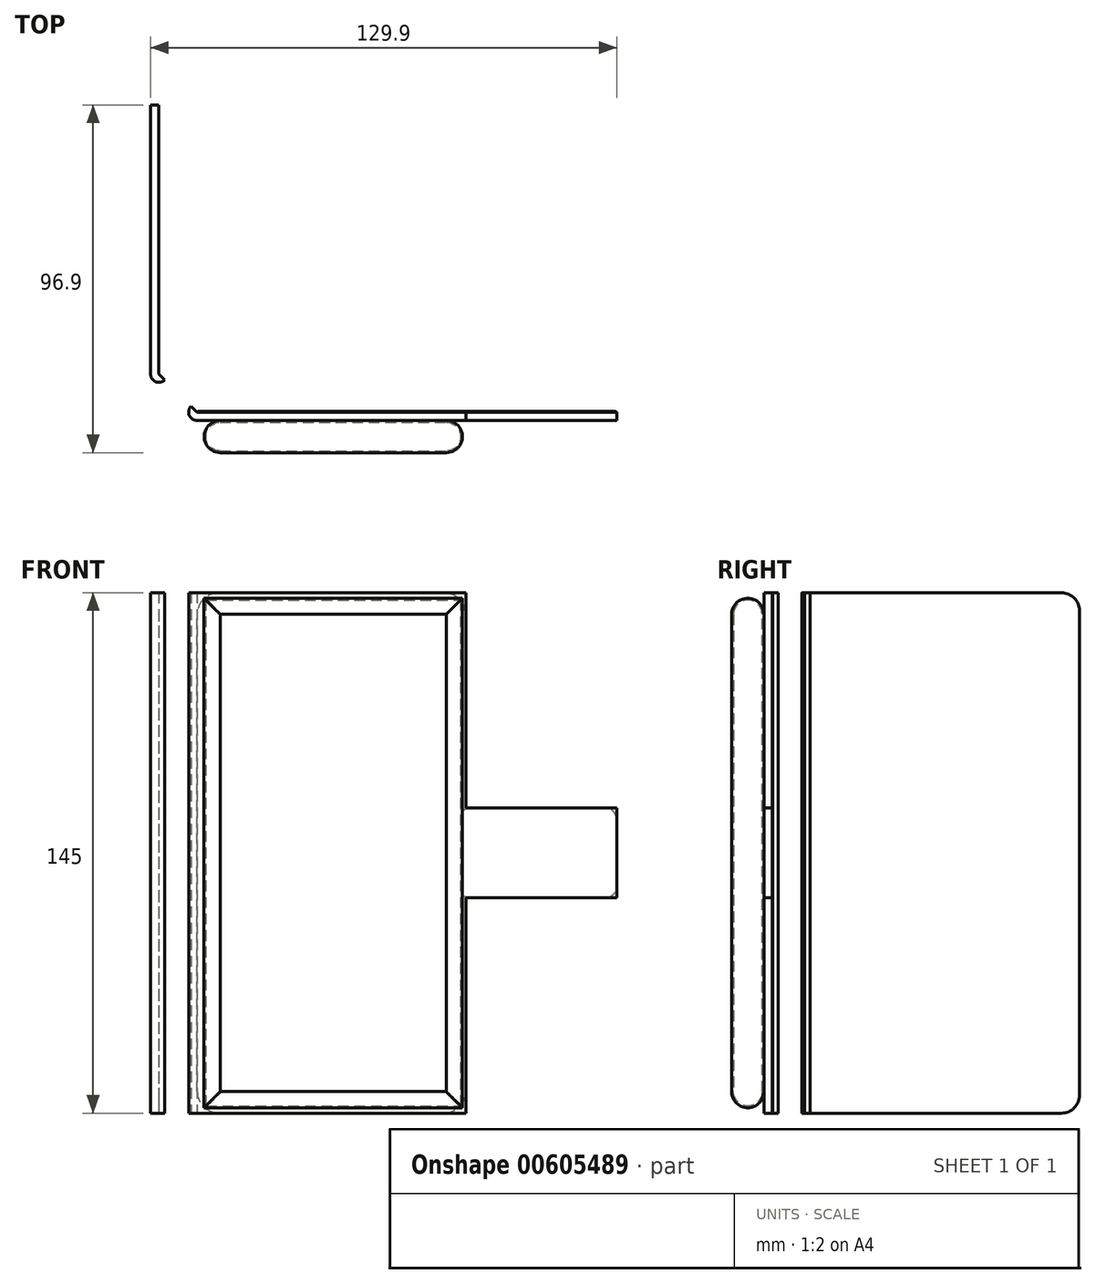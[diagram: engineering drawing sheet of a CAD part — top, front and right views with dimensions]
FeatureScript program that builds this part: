
annotation { "Feature Type Name" : "Feature", "Feature Type Description" : "" }
export const myFeature = defineFeature(function(context is Context, id is Id, definition is map)
    precondition{}
    {
        {
            var Q0;
            Q0=qCreatedBy(makeId("Front.planeOp"),FACE);
            var sketch = newSketch(context, id + "F0", { "sketchPlane" : qUnion([Q0])});
            skLineSegment(sketch, "E0.bottom", {"start": v(36, -71) * mm, "end": v(-36, -71) * mm});
            skLineSegment(sketch, "E0.top", {"start": v(36, 71) * mm, "end": v(-36, 71) * mm});
            skLineSegment(sketch, "E0.left", {"start": v(36, -71) * mm, "end": v(36, 71) * mm});
            skLineSegment(sketch, "E0.right", {"start": v(-36, -71) * mm, "end": v(-36, 71) * mm});
            skPoint(sketch, "E0.middle", {"position": v(0, 0) * mm});
            skSolve(sketch);
        }
        {
            var Q0;
            Q0=makeQuery(id+"F0.imprint","IMPRINT",FACE,{"disambiguationData":[TD([[makeQuery(id+"F0.imprint","IMPRINT",EDGE,{"derivedFrom":sQuery(id+"F0.wireOp",EDGE,"E0.bottom")}),-1.0]])]});
            extrude(context, id + "F1", {"entities" : qUnion([Q0]), "depth" : 9 * mm, "offsetDistance" : 25 * mm});
        }
        {
            var Q0;
            Q0=makeQuery(id+"F1.opExtrude","SWEPT_FACE",FACE,{"disambiguationData":[OSD([sQuery(id+"F0.wireOp",EDGE,"E0.bottom")])]});
            var sketch = newSketch(context, id + "F2", { "sketchPlane" : qUnion([Q0])});
            skLineSegment(sketch, "E1", {"start": v(-36, 4.5) * mm, "end": v(-31.5, 4.5) * mm, "construction": true});
            skArc(sketch, "E2", {"start": v(-31.5, 9) * mm, "mid": v(-36, 4.5) * mm, "end": v(-31.5, 0) * mm});
            skLineSegment(sketch, "E3.bottom", {"start": v(-36, 9) * mm, "end": v(-31.5, 9) * mm});
            skLineSegment(sketch, "E3.top", {"start": v(-36, 0) * mm, "end": v(-31.5, 0) * mm});
            skLineSegment(sketch, "E3.left", {"start": v(-36, 9) * mm, "end": v(-36, 0) * mm, "construction": true});
            skPoint(sketch, "E3.right.end.orphan", {"position": v(-27, 0) * mm});
            skPoint(sketch, "E3.right.start.orphan", {"position": v(-27, 9) * mm});
            skLineSegment(sketch, "E4.bottom", {"start": v(-36, 9) * mm, "end": v(-36.25, 9) * mm});
            skLineSegment(sketch, "E4.top", {"start": v(-36, 0) * mm, "end": v(-36.25, 0) * mm});
            skLineSegment(sketch, "E4.left", {"start": v(-36, 9) * mm, "end": v(-36, 0) * mm});
            skLineSegment(sketch, "E4.right", {"start": v(-36.25, 9) * mm, "end": v(-36.25, 0) * mm});
            skLineSegment(sketch, "E5", {"start": v(0, 9) * mm, "end": v(0, 0) * mm, "construction": true});
            skLineSegment(sketch, "E6.MirrorCS", {"start": v(36, 9) * mm, "end": v(36.25, 9) * mm});
            skLineSegment(sketch, "E7.MirrorCS", {"start": v(36, 0) * mm, "end": v(36.25, 0) * mm});
            skLineSegment(sketch, "E8.MirrorCS", {"start": v(36, 9) * mm, "end": v(36, 0) * mm});
            skLineSegment(sketch, "E9.MirrorCS", {"start": v(36.25, 9) * mm, "end": v(36.25, 0) * mm});
            skPoint(sketch, "E10.MirrorP", {"position": v(27, 9) * mm});
            skLineSegment(sketch, "E11.MirrorCS", {"start": v(36, 4.5) * mm, "end": v(31.5, 4.5) * mm, "construction": true});
            skPoint(sketch, "E12.MirrorP", {"position": v(27, 0) * mm});
            skArc(sketch, "E13.MirrorCS", {"start": v(31.5, 9) * mm, "mid": v(36, 4.5) * mm, "end": v(31.5, 0) * mm});
            skLineSegment(sketch, "E14.MirrorCS", {"start": v(36, 9) * mm, "end": v(31.5, 9) * mm});
            skLineSegment(sketch, "E15.MirrorCS", {"start": v(36, 9) * mm, "end": v(36, 0) * mm, "construction": true});
            skLineSegment(sketch, "E16.MirrorCS", {"start": v(36, 0) * mm, "end": v(31.5, 0) * mm});
            skLineSegment(sketch, "E17.MirrorCS", {"start": v(-72, 9) * mm, "end": v(-72, 0) * mm, "construction": true});
            skSolve(sketch);
        }
        {
            var Q0;
            {var subQ0=sQuery(id+"F2.wireOp",EDGE,"E3.bottom");Q0=makeQuery(id+"F2.imprint","IMPRINT",FACE,{"disambiguationData":[TD([[makeQuery(id+"F2.imprint","IMPRINT",EDGE,{"derivedFrom":subQ0}),1.0]])]});}
            var Q1;
            {var subQ3=sQuery(id+"F2.wireOp",EDGE,"E4.bottom");Q1=makeQuery(id+"F2.imprint","IMPRINT",FACE,{"disambiguationData":[TD([[makeQuery(id+"F2.imprint","IMPRINT",EDGE,{"derivedFrom":subQ3}),1.0]])]});}
            var Q2;
            {var subQ0=sQuery(id+"F2.wireOp",EDGE,"E3.top");Q2=makeQuery(id+"F2.imprint","IMPRINT",FACE,{"disambiguationData":[TD([[makeQuery(id+"F2.imprint","IMPRINT",EDGE,{"derivedFrom":subQ0}),-1.0]])]});}
            var Q3;
            {var subQ0=sQuery(id+"F2.wireOp",EDGE,"E14.MirrorCS");Q3=makeQuery(id+"F2.imprint","IMPRINT",FACE,{"disambiguationData":[TD([[makeQuery(id+"F2.imprint","IMPRINT",EDGE,{"derivedFrom":subQ0}),1.0]])]});}
            var Q4;
            {var subQ3=sQuery(id+"F2.wireOp",EDGE,"E6.MirrorCS");Q4=makeQuery(id+"F2.imprint","IMPRINT",FACE,{"disambiguationData":[TD([[makeQuery(id+"F2.imprint","IMPRINT",EDGE,{"derivedFrom":subQ3}),-1.0]])]});}
            var Q5;
            {var subQ0=sQuery(id+"F2.wireOp",EDGE,"E16.MirrorCS");Q5=makeQuery(id+"F2.imprint","IMPRINT",FACE,{"disambiguationData":[TD([[makeQuery(id+"F2.imprint","IMPRINT",EDGE,{"derivedFrom":subQ0}),-1.0]])]});}
            extrude(context, id + "F3", {"entities" : qUnion([Q0, Q1, Q2, Q3, Q4, Q5]), "operationType" : NewBodyOperationType.REMOVE, "endBound" : BoundingType.THROUGH_ALL, "oppositeDirection" : true, "depth" : 25 * mm, "offsetDistance" : 25 * mm});
        }
        {
            var Q0;
            Q0=qCreatedBy(makeId("Right.planeOp"),FACE);
            cPlane(context, id + "F4", {"entities" : qUnion([Q0]), "cplaneType" : CPlaneType.OFFSET, "offset" : 45 * mm, "width" : 150 * mm, "height" : 150 * mm});
        }
        {
            var Q0;
            Q0=qCreatedBy(id+"F4.planeOp",FACE);
            var sketch = newSketch(context, id + "F5", { "sketchPlane" : qUnion([Q0])});
            skLineSegment(sketch, "E18", {"start": v(0, 0) * mm, "end": v(-9, 0) * mm, "construction": true});
            skLineSegment(sketch, "E19.0", {"start": v(-9, -71) * mm, "end": v(0, -71) * mm, "construction": true});
            skLineSegment(sketch, "E20", {"start": v(-4.5, -71) * mm, "end": v(-4.5, -66.5) * mm, "construction": true});
            skPoint(sketch, "E21.middle", {"position": v(-4.5, -66.5) * mm});
            skLineSegment(sketch, "E22.bottom", {"start": v(-9, -71.25) * mm, "end": v(0, -71.25) * mm});
            skLineSegment(sketch, "E22.left", {"start": v(-9, -71.25) * mm, "end": v(-9, -66.5) * mm});
            skLineSegment(sketch, "E22.right", {"start": v(0, -71.25) * mm, "end": v(0, -66.5) * mm});
            skArc(sketch, "E23", {"start": v(-9, -66.5) * mm, "mid": v(-4.5, -71) * mm, "end": v(0, -66.5) * mm});
            skPoint(sketch, "E22.top.start.orphan", {"position": v(-9, -61.75) * mm});
            skPoint(sketch, "E24.orphan", {"position": v(0, -61.75) * mm});
            skLineSegment(sketch, "E25.MirrorCS", {"start": v(-9, 71.25) * mm, "end": v(0, 71.25) * mm});
            skLineSegment(sketch, "E26.MirrorCS", {"start": v(-4.5, 71) * mm, "end": v(-4.5, 66.5) * mm, "construction": true});
            skPoint(sketch, "E27.MirrorP", {"position": v(-4.5, 66.5) * mm});
            skPoint(sketch, "E28.MirrorP", {"position": v(-9, 61.75) * mm});
            skPoint(sketch, "E29.MirrorP", {"position": v(0, 61.75) * mm});
            skArc(sketch, "E30.MirrorCS", {"start": v(-9, 66.5) * mm, "mid": v(-4.5, 71) * mm, "end": v(0, 66.5) * mm});
            skLineSegment(sketch, "E31.MirrorCS", {"start": v(-9, 71.25) * mm, "end": v(-9, 66.5) * mm});
            skLineSegment(sketch, "E32.MirrorCS", {"start": v(0, 71.25) * mm, "end": v(0, 66.5) * mm});
            skLineSegment(sketch, "E33.MirrorCS", {"start": v(-9, 71) * mm, "end": v(0, 71) * mm, "construction": true});
            skSolve(sketch);
        }
        {
            var Q0;
            Q0=makeQuery(id+"F5.imprint","IMPRINT",FACE,{"disambiguationData":[TD([[makeQuery(id+"F5.imprint","IMPRINT",EDGE,{"derivedFrom":sQuery(id+"F5.wireOp",EDGE,"E22.bottom")}),1.0]])]});
            var Q1;
            Q1=makeQuery(id+"F5.imprint","IMPRINT",FACE,{"disambiguationData":[TD([[makeQuery(id+"F5.imprint","IMPRINT",EDGE,{"derivedFrom":sQuery(id+"F5.wireOp",EDGE,"E25.MirrorCS")}),-1.0]])]});
            extrude(context, id + "F6", {"entities" : qUnion([Q0, Q1]), "operationType" : NewBodyOperationType.REMOVE, "endBound" : BoundingType.THROUGH_ALL, "oppositeDirection" : true, "depth" : 25 * mm, "offsetDistance" : 25 * mm});
        }
        {
            var Q0;
            Q0=makeQuery(id+"F1.opExtrude","CAP_FACE",FACE,{"disambiguationData":[OSD([sQuery(id+"F0.wireOp",EDGE,"E0.bottom"),sQuery(id+"F0.wireOp",EDGE,"E0.top"),sQuery(id+"F0.wireOp",EDGE,"E0.left"),sQuery(id+"F0.wireOp",EDGE,"E0.right")])],"isStart":false});
            shell(context, id + "F7", {"entities" : qUnion([Q0]), "thickness" : 0.5 * mm});
        }
        {
            var Q0;
            Q0=qCreatedBy(makeId("Front.planeOp"),FACE);
            var sketch = newSketch(context, id + "F8", { "sketchPlane" : qUnion([Q0])});
            skLineSegment(sketch, "E34.0.0", {"start": v(36, -71) * mm, "end": v(36, 71) * mm});
            skLineSegment(sketch, "E34.0.1", {"start": v(36, 71) * mm, "end": v(-36, 71) * mm});
            skLineSegment(sketch, "E34.0.2", {"start": v(-36, 71) * mm, "end": v(-36, -71) * mm});
            skLineSegment(sketch, "E34.0.3", {"start": v(-36, -71) * mm, "end": v(36, -71) * mm});
            skLineSegment(sketch, "E35.0.0", {"start": v(36, -71) * mm, "end": v(36, 71) * mm, "construction": true});
            skLineSegment(sketch, "E35.0.1", {"start": v(36, 71) * mm, "end": v(-36, 71) * mm, "construction": true});
            skLineSegment(sketch, "E35.0.2", {"start": v(-36, 71) * mm, "end": v(-36, -71) * mm, "construction": true});
            skLineSegment(sketch, "E35.0.3", {"start": v(-36, -71) * mm, "end": v(36, -71) * mm, "construction": true});
            skLineSegment(sketch, "E36", {"start": v(0, 0) * mm, "end": v(36, 0) * mm});
            skLineSegment(sketch, "E37", {"start": v(36, 0) * mm, "end": v(37, 0) * mm});
            skLineSegment(sketch, "E38", {"start": v(37, 0) * mm, "end": v(-128, 0) * mm, "construction": true});
            skLineSegment(sketch, "E39", {"start": v(-45.5, 0) * mm, "end": v(-45.5, 145) * mm, "construction": true});
            skPoint(sketch, "E39.endSnap0", {"position": v(-45.5, 0) * mm});
            skLineSegment(sketch, "E40", {"start": v(-45.5, 72.5) * mm, "end": v(-45.5, -72.5) * mm, "construction": true});
            skLineSegment(sketch, "E41.bottom", {"start": v(-128, -72.5) * mm, "end": v(37, -72.5) * mm});
            skLineSegment(sketch, "E41.top", {"start": v(-128, 72.5) * mm, "end": v(37, 72.5) * mm});
            skLineSegment(sketch, "E41.left", {"start": v(-128, -72.5) * mm, "end": v(-128, 72.5) * mm});
            skLineSegment(sketch, "E41.right", {"start": v(37, -72.5) * mm, "end": v(37, 72.5) * mm});
            skLineSegment(sketch, "E42.bottom", {"start": v(79, -12.5) * mm, "end": v(-5, -12.5) * mm});
            skLineSegment(sketch, "E42.top", {"start": v(79, 12.5) * mm, "end": v(-5, 12.5) * mm});
            skLineSegment(sketch, "E42.left", {"start": v(79, -12.5) * mm, "end": v(79, 12.5) * mm});
            skLineSegment(sketch, "E42.right", {"start": v(-5, -12.5) * mm, "end": v(-5, 12.5) * mm});
            skPoint(sketch, "E42.middle", {"position": v(37, 0) * mm});
            skLineSegment(sketch, "E43.bottom", {"start": v(-53, 72.5) * mm, "end": v(-38, 72.5) * mm});
            skLineSegment(sketch, "E43.top", {"start": v(-53, -72.5) * mm, "end": v(-38, -72.5) * mm});
            skLineSegment(sketch, "E43.left", {"start": v(-53, 72.5) * mm, "end": v(-53, -72.5) * mm});
            skLineSegment(sketch, "E43.right", {"start": v(-38, 72.5) * mm, "end": v(-38, -72.5) * mm});
            skSolve(sketch);
        }
        {
            var Q0;
            {var subQ10=sQuery(id+"F8.wireOp",EDGE,"E34.0.1");Q0=makeQuery(id+"F8.imprint","IMPRINT",FACE,{"disambiguationData":[TD([[makeQuery(id+"F8.imprint","IMPRINT",EDGE,{"derivedFrom":subQ10}),-1.0]])]});}
            var Q1;
            {var subQ0=sQuery(id+"F8.wireOp",EDGE,"E34.0.1");Q1=makeQuery(id+"F8.imprint","IMPRINT",FACE,{"disambiguationData":[TD([[makeQuery(id+"F8.imprint","IMPRINT",EDGE,{"derivedFrom":subQ0}),1.0]])]});}
            var Q2;
            {var subQ0=sQuery(id+"F8.wireOp",EDGE,"E42.right");Q2=makeQuery(id+"F8.imprint","IMPRINT",FACE,{"disambiguationData":[TD([[makeQuery(id+"F8.imprint","IMPRINT",EDGE,{"derivedFrom":subQ0}),-1.0]])]});}
            var Q3;
            {var subQ0=sQuery(id+"F8.wireOp",EDGE,"E37");Q3=makeQuery(id+"F8.imprint","IMPRINT",FACE,{"disambiguationData":[TD([[makeQuery(id+"F8.imprint","IMPRINT",EDGE,{"derivedFrom":subQ0}),-1.0]])]});}
            var Q4;
            {var subQ0=sQuery(id+"F8.wireOp",EDGE,"E37");Q4=makeQuery(id+"F8.imprint","IMPRINT",FACE,{"disambiguationData":[TD([[makeQuery(id+"F8.imprint","IMPRINT",EDGE,{"derivedFrom":subQ0}),1.0]])]});}
            var Q5;
            {var subQ0=sQuery(id+"F8.wireOp",EDGE,"E42.left");Q5=makeQuery(id+"F8.imprint","IMPRINT",FACE,{"disambiguationData":[TD([[makeQuery(id+"F8.imprint","IMPRINT",EDGE,{"derivedFrom":subQ0}),1.0]])]});}
            extrude(context, id + "F9", {"entities" : qUnion([Q0, Q1, Q2, Q3, Q4, Q5]), "oppositeDirection" : true, "depth" : 2.5 * mm, "offsetDistance" : 25 * mm});
        }
        {
            var Q0;
            Q0=makeQuery(id+"F9.opExtrude","CAP_FACE",FACE,{"disambiguationData":[OSD([sQuery(id+"F8.wireOp",EDGE,"E41.bottom"),sQuery(id+"F8.wireOp",EDGE,"E41.top"),sQuery(id+"F8.wireOp",EDGE,"E41.left"),sQuery(id+"F8.wireOp",EDGE,"E41.right"),sQuery(id+"F8.wireOp",EDGE,"E42.bottom"),sQuery(id+"F8.wireOp",EDGE,"E42.top"),sQuery(id+"F8.wireOp",EDGE,"E42.left")])],"isStart":true});
            var Q1;
            Q1=makeQuery(id+"F9.opExtrude","CAP_FACE",FACE,{"disambiguationData":[OSD([sQuery(id+"F8.wireOp",EDGE,"E41.bottom"),sQuery(id+"F8.wireOp",EDGE,"E41.top"),sQuery(id+"F8.wireOp",EDGE,"E41.left"),sQuery(id+"F8.wireOp",EDGE,"E41.right"),sQuery(id+"F8.wireOp",EDGE,"E42.bottom"),sQuery(id+"F8.wireOp",EDGE,"E42.top"),sQuery(id+"F8.wireOp",EDGE,"E42.left")])],"isStart":false});
            fillet(context, id + "F10", {"entities" : qUnion([Q0, Q1]), "radius" : 0.5 * mm, "tangentPropagation" : true, "allowEdgeOverflow" : false});
        }
        {
            var Q0;
            Q0=makeQuery(id+"F9.opExtrude","SWEPT_EDGE",EDGE,{"disambiguationData":[OSD([sQuery(id+"F8.wireOp",EDGE,"E42.top"),sQuery(id+"F8.wireOp",EDGE,"E42.left")])]});
            var Q1;
            Q1=makeQuery(id+"F9.opExtrude","SWEPT_EDGE",EDGE,{"disambiguationData":[OSD([sQuery(id+"F8.wireOp",EDGE,"E42.bottom"),sQuery(id+"F8.wireOp",EDGE,"E42.left")])]});
            fillet(context, id + "F11", {"entities" : qUnion([Q0, Q1]), "radius" : 3 * mm, "tangentPropagation" : true, "allowEdgeOverflow" : false});
        }
        {
            var Q0;
            Q0=makeQuery(id+"F9.opExtrude","SWEPT_EDGE",EDGE,{"disambiguationData":[OSD([sQuery(id+"F8.wireOp",EDGE,"E41.top"),sQuery(id+"F8.wireOp",EDGE,"E41.right")])]});
            var Q1;
            Q1=makeQuery(id+"F9.opExtrude","SWEPT_EDGE",EDGE,{"disambiguationData":[OSD([sQuery(id+"F8.wireOp",EDGE,"E41.top"),sQuery(id+"F8.wireOp",EDGE,"E41.left")])]});
            var Q2;
            Q2=makeQuery(id+"F9.opExtrude","SWEPT_EDGE",EDGE,{"disambiguationData":[OSD([sQuery(id+"F8.wireOp",EDGE,"E41.bottom"),sQuery(id+"F8.wireOp",EDGE,"E41.left")])]});
            var Q3;
            Q3=makeQuery(id+"F9.opExtrude","SWEPT_EDGE",EDGE,{"disambiguationData":[OSD([sQuery(id+"F8.wireOp",EDGE,"E41.bottom"),sQuery(id+"F8.wireOp",EDGE,"E41.right")])]});
            fillet(context, id + "F12", {"entities" : qUnion([Q0, Q1, Q2, Q3]), "radius" : 6 * mm, "tangentPropagation" : true, "allowEdgeOverflow" : false});
        }
        {
            var Q0;
            Q0=qCreatedBy(makeId("Top.planeOp"),FACE);
            var sketch = newSketch(context, id + "F13", { "sketchPlane" : qUnion([Q0])});
            skLineSegment(sketch, "E44", {"start": v(-38, 0) * mm, "end": v(-36, 0) * mm});
            skLineSegment(sketch, "E45.bottom", {"start": v(-38, 0) * mm, "end": v(37, 0) * mm});
            skLineSegment(sketch, "E45.top", {"start": v(-38, 2.3) * mm, "end": v(37, 2.3) * mm});
            skLineSegment(sketch, "E45.left", {"start": v(-38, 0) * mm, "end": v(-38, 2.3) * mm});
            skLineSegment(sketch, "E45.right", {"start": v(37, 0) * mm, "end": v(37, 2.3) * mm});
            skCircle(sketch, "E46", {"center": v(-38, 2.3) * mm, "radius": 2.3 * mm});
            skLineSegment(sketch, "E47", {"start": v(-50.23, 11.28) * mm, "end": v(-39.63, 0.67) * mm});
            skLineSegment(sketch, "E48.0", {"start": v(-48.6, 12.9) * mm, "end": v(-38, 2.3) * mm});
            skCircle(sketch, "E49", {"center": v(-48.6, 12.9) * mm, "radius": 2.3 * mm});
            skLineSegment(sketch, "E50", {"start": v(-50.23, 11.28) * mm, "end": v(-48.6, 12.9) * mm});
            skLineSegment(sketch, "E51.bottom", {"start": v(-48.6, 12.9) * mm, "end": v(-50.9, 12.9) * mm});
            skLineSegment(sketch, "E51.top", {"start": v(-48.6, 87.9) * mm, "end": v(-50.9, 87.9) * mm});
            skLineSegment(sketch, "E51.left", {"start": v(-48.6, 12.9) * mm, "end": v(-48.6, 87.9) * mm});
            skLineSegment(sketch, "E51.right", {"start": v(-50.9, 12.9) * mm, "end": v(-50.9, 87.9) * mm});
            skPoint(sketch, "E52.oppositeSnap0", {"position": v(-0.5, 2.3) * mm});
            skLineSegment(sketch, "E52.bottom", {"start": v(37, 0) * mm, "end": v(79, 0) * mm});
            skLineSegment(sketch, "E52.top", {"start": v(37, 2.3) * mm, "end": v(79, 2.3) * mm});
            skLineSegment(sketch, "E52.right", {"start": v(79, 0) * mm, "end": v(79, 2.3) * mm});
            skSolve(sketch);
        }
        {
            var Q0;
            {var subQ4=sQuery(id+"F13.wireOp",EDGE,"E51.top");Q0=makeQuery(id+"F13.imprint","IMPRINT",FACE,{"disambiguationData":[TD([[makeQuery(id+"F13.imprint","IMPRINT",EDGE,{"derivedFrom":subQ4}),1.0]])]});}
            var Q1;
            {var subQ0=sQuery(id+"F13.wireOp",EDGE,"E51.bottom");Q1=makeQuery(id+"F13.imprint","IMPRINT",FACE,{"disambiguationData":[TD([[makeQuery(id+"F13.imprint","IMPRINT",EDGE,{"derivedFrom":subQ0}),-1.0]])]});}
            var Q2;
            {var subQ0=sQuery(id+"F13.wireOp",EDGE,"E50");Q2=makeQuery(id+"F13.imprint","IMPRINT",FACE,{"disambiguationData":[TD([[makeQuery(id+"F13.imprint","IMPRINT",EDGE,{"derivedFrom":subQ0}),1.0]])]});}
            var Q3;
            {var subQ0=sQuery(id+"F13.wireOp",EDGE,"E47");Q3=makeQuery(id+"F13.imprint","IMPRINT",FACE,{"disambiguationData":[TD([[makeQuery(id+"F13.imprint","IMPRINT",EDGE,{"derivedFrom":subQ0}),1.0]])]});}
            var Q4;
            {var subQ0=sQuery(id+"F13.wireOp",EDGE,"E50");Q4=makeQuery(id+"F13.imprint","IMPRINT",FACE,{"disambiguationData":[TD([[makeQuery(id+"F13.imprint","IMPRINT",EDGE,{"derivedFrom":subQ0}),-1.0]])]});}
            var Q5;
            {var subQ0=sQuery(id+"F13.wireOp",EDGE,"E45.left");Q5=makeQuery(id+"F13.imprint","IMPRINT",FACE,{"disambiguationData":[TD([[makeQuery(id+"F13.imprint","IMPRINT",EDGE,{"derivedFrom":subQ0}),1.0]])]});}
            var Q6;
            {var subQ0=sQuery(id+"F13.wireOp",EDGE,"E45.left");Q6=makeQuery(id+"F13.imprint","IMPRINT",FACE,{"disambiguationData":[TD([[makeQuery(id+"F13.imprint","IMPRINT",EDGE,{"derivedFrom":subQ0}),-1.0]])]});}
            var Q7;
            {var subQ3=sQuery(id+"F13.wireOp",EDGE,"E45.right");Q7=makeQuery(id+"F13.imprint","IMPRINT",FACE,{"disambiguationData":[TD([[makeQuery(id+"F13.imprint","IMPRINT",EDGE,{"derivedFrom":subQ3}),1.0]])]});}
            extrude(context, id + "F14", {"entities" : qUnion([Q0, Q1, Q2, Q3, Q4, Q5, Q6, Q7]), "endBound" : BoundingType.SYMMETRIC, "depth" : 145 * mm, "offsetDistance" : 25 * mm});
        }
        {
            var Q0;
            Q0=makeQuery(id+"F13.imprint","IMPRINT",FACE,{"disambiguationData":[TD([[makeQuery(id+"F13.imprint","IMPRINT",EDGE,{"derivedFrom":sQuery(id+"F13.wireOp",EDGE,"E52.bottom")}),1.0]])]});
            extrude(context, id + "F15", {"entities" : qUnion([Q0]), "operationType" : NewBodyOperationType.ADD, "endBound" : BoundingType.SYMMETRIC, "depth" : 25 * mm, "offsetDistance" : 25 * mm});
        }
        {
            var Q0;
            Q0=makeQuery(id+"F14.opExtrude","CAP_EDGE",EDGE,{"disambiguationData":[OSD([sQuery(id+"F13.wireOp",EDGE,"E51.top")])],"isStart":false});
            var Q1;
            Q1=makeQuery(id+"F14.opExtrude","CAP_EDGE",EDGE,{"disambiguationData":[OSD([sQuery(id+"F13.wireOp",EDGE,"E51.top")])],"isStart":true});
            var Q2;
            Q2=makeQuery(id+"F14.opExtrude","CAP_EDGE",EDGE,{"disambiguationData":[OSD([sQuery(id+"F13.wireOp",EDGE,"E45.right")])],"isStart":false});
            var Q3;
            Q3=makeQuery(id+"F14.opExtrude","CAP_EDGE",EDGE,{"disambiguationData":[OSD([sQuery(id+"F13.wireOp",EDGE,"E45.right")])],"isStart":true});
            var Q4;
            Q4=makeQuery(id+"F15.opExtrude","CAP_EDGE",EDGE,{"disambiguationData":[OSD([sQuery(id+"F13.wireOp",EDGE,"E52.right")])],"isStart":true});
            var Q5;
            Q5=makeQuery(id+"F15.opExtrude","CAP_EDGE",EDGE,{"disambiguationData":[OSD([sQuery(id+"F13.wireOp",EDGE,"E52.right")])],"isStart":false});
            fillet(context, id + "F16", {"entities" : qUnion([Q0, Q1, Q2, Q3, Q4, Q5]), "radius" : 5 * mm, "tangentPropagation" : true, "allowEdgeOverflow" : false});
        }
    });
